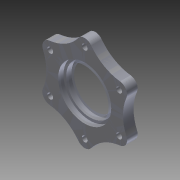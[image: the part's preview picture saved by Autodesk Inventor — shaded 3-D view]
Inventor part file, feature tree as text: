
AUTODESK INVENTOR PART (.ipt)
format: ipt  version: 2012 (Build 160160000, 160)  size: 295,424 bytes
history: native  units: in
note: dims shown in document units (in); Inventor stores cm internally (conversion verified against a paired STEP export)
features: extrude x4, other x3, sketch x2
ambient origin geometry x8: Origin, YZ Plane, XZ Plane, XY Plane, X Axis, Y Axis, Z Axis, Center Point
bodies: Solid1 (feature_tree)
feature tree (9):
  other  "Shaft Collar.IGS1"
  sketch  "Sketch2"  dims[d0=0.25in d1=0.0in d2=0.125in d3=0.0in]
  extrude  "Extrusion1"  Depth=0.125in TaperAngle=0.0deg
  extrude  "Extrusion2"  Depth=0.125in TaperAngle=0.0deg
  sketch  "Sketch3"  dims[d4=1.25in d5=0.125in d6=0.0in d7=0.125in d8=0.0in]
  extrude  "Extrusion3"  Depth=0.125in TaperAngle=0.0deg
  extrude  "Extrusion4"  [1 undecoded]
  other  "Composite1"
  other  "Srf1"
note: 1 required parameter value undecoded (feature->parameter linkage not recoverable at this tier; creation-order binding heuristic only, values carry confidence <= 0.55)
